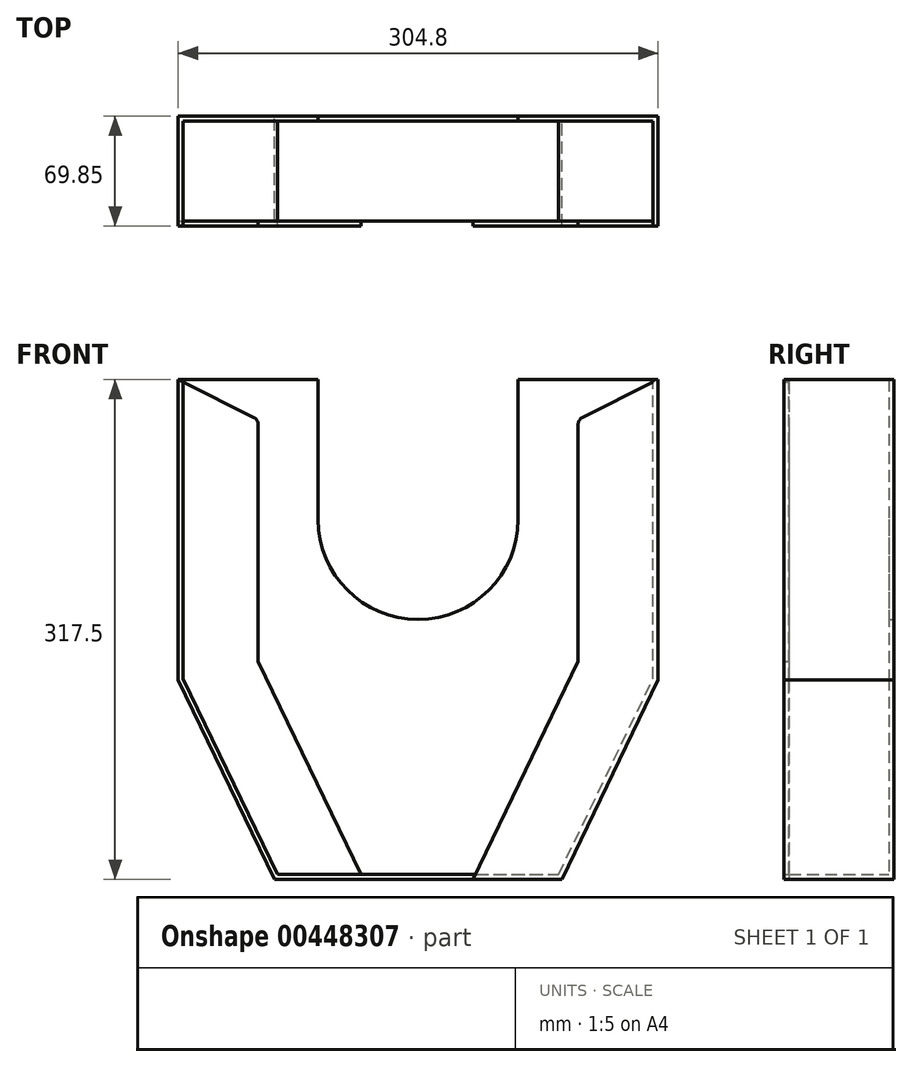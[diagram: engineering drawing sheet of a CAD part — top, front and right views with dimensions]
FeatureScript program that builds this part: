
annotation { "Feature Type Name" : "Feature", "Feature Type Description" : "" }
export const myFeature = defineFeature(function(context is Context, id is Id, definition is map)
    precondition{}
    {
        {
            var Q0;
            Q0=qCreatedBy(makeId("Front.planeOp"),FACE);
            var sketch = newSketch(context, id + "F0", { "sketchPlane" : qUnion([Q0])});
            skLineSegment(sketch, "E0", {"start": v(-244.47, 127.9) * mm, "end": v(-91.22, -189.6) * mm});
            skLineSegment(sketch, "E1", {"start": v(-91.22, -189.6) * mm, "end": v(91.22, -189.6) * mm});
            skLineSegment(sketch, "E2", {"start": v(91.22, -189.6) * mm, "end": v(244.47, 127.9) * mm});
            skLineSegment(sketch, "E3", {"start": v(244.48, 127.9) * mm, "end": v(-244.48, 127.9) * mm});
            skLineSegment(sketch, "E4.bottom", {"start": v(-63.5, 127.9) * mm, "end": v(63.5, 127.9) * mm});
            skLineSegment(sketch, "E4.top", {"start": v(-63.5, 39) * mm, "end": v(63.5, 39) * mm});
            skLineSegment(sketch, "E4.left", {"start": v(-63.5, 127.9) * mm, "end": v(-63.5, 39) * mm});
            skLineSegment(sketch, "E4.right", {"start": v(63.5, 127.9) * mm, "end": v(63.5, 39) * mm});
            skArc(sketch, "E5", {"start": v(-63.5, 39) * mm, "mid": v(0, -24.5) * mm, "end": v(63.5, 39) * mm});
            skCircle(sketch, "E6", {"center": v(0, -49.9) * mm, "radius": 139.7 * mm});
            skLineSegment(sketch, "E7", {"start": v(-152.4, -62.86) * mm, "end": v(-152.4, 127.9) * mm});
            skLineSegment(sketch, "E8", {"start": v(0, 127.9) * mm, "end": v(0, -189.6) * mm});
            skLineSegment(sketch, "E9.MirrorCS", {"start": v(152.4, -62.86) * mm, "end": v(152.4, 127.9) * mm});
            skSolve(sketch);
        }
        {
            var Q0;
            {var subQ1=sQuery(id+"F0.wireOp",EDGE,"E4.right");var subQ3=sQuery(id+"F0.wireOp",EDGE,"E6");var subQ4=makeQuery(id+"F0.imprint","INTERSECT",VERTEX,{"derivedFrom":[subQ1,subQ3]});Q0=makeQuery(id+"F0.imprint","IMPRINT",FACE,{"disambiguationData":[TD([[makeQuery(id+"F0.imprint","IMPRINT",EDGE,{"disambiguationData":[TD([[subQ4,-1.0]])],"derivedFrom":subQ1}),1.0]])]});}
            var Q1;
            {var subQ1=sQuery(id+"F0.wireOp",EDGE,"E4.left");var subQ3=sQuery(id+"F0.wireOp",EDGE,"E6");var subQ4=makeQuery(id+"F0.imprint","INTERSECT",VERTEX,{"derivedFrom":[subQ1,subQ3]});Q1=makeQuery(id+"F0.imprint","IMPRINT",FACE,{"disambiguationData":[TD([[makeQuery(id+"F0.imprint","IMPRINT",EDGE,{"disambiguationData":[TD([[subQ4,-1.0]])],"derivedFrom":subQ1}),-1.0]])]});}
            var Q2;
            {var subQ5=sQuery(id+"F0.wireOp",EDGE,"E7");Q2=makeQuery(id+"F0.imprint","IMPRINT",FACE,{"disambiguationData":[TD([[makeQuery(id+"F0.imprint","IMPRINT",EDGE,{"derivedFrom":subQ5}),-1.0]])]});}
            var Q3;
            {var subQ5=sQuery(id+"F0.wireOp",EDGE,"E9.MirrorCS");Q3=makeQuery(id+"F0.imprint","IMPRINT",FACE,{"disambiguationData":[TD([[makeQuery(id+"F0.imprint","IMPRINT",EDGE,{"derivedFrom":subQ5}),1.0]])]});}
            var Q4;
            {var subQ5=sQuery(id+"F0.wireOp",EDGE,"E7");Q4=makeQuery(id+"F0.imprint","IMPRINT",FACE,{"disambiguationData":[TD([[makeQuery(id+"F0.imprint","IMPRINT",EDGE,{"derivedFrom":subQ5}),-1.0]])]});}
            var Q5;
            {var subQ5=sQuery(id+"F0.wireOp",EDGE,"E9.MirrorCS");Q5=makeQuery(id+"F0.imprint","IMPRINT",FACE,{"disambiguationData":[TD([[makeQuery(id+"F0.imprint","IMPRINT",EDGE,{"derivedFrom":subQ5}),1.0]])]});}
            var Q6;
            {var subQ1=sQuery(id+"F0.wireOp",EDGE,"E4.right");var subQ3=sQuery(id+"F0.wireOp",EDGE,"E6");var subQ4=makeQuery(id+"F0.imprint","INTERSECT",VERTEX,{"derivedFrom":[subQ1,subQ3]});Q6=makeQuery(id+"F0.imprint","IMPRINT",FACE,{"disambiguationData":[TD([[makeQuery(id+"F0.imprint","IMPRINT",EDGE,{"disambiguationData":[TD([[subQ4,-1.0]])],"derivedFrom":subQ1}),1.0]])]});}
            extrude(context, id + "F1", {"entities" : qUnion([Q0, Q1, Q2, Q3, Q4, Q5, Q6]), "depth" : 3.17 * mm});
        }
        {
            var Q0;
            Q0=makeQuery(id+"F1.opExtrude","CAP_FACE",FACE,{"disambiguationData":[OSD([sQuery(id+"F0.wireOp",EDGE,"E0"),sQuery(id+"F0.wireOp",EDGE,"E1"),sQuery(id+"F0.wireOp",EDGE,"E2"),sQuery(id+"F0.wireOp",EDGE,"E3"),sQuery(id+"F0.wireOp",EDGE,"E4.left"),sQuery(id+"F0.wireOp",EDGE,"E4.right"),sQuery(id+"F0.wireOp",EDGE,"E5"),sQuery(id+"F0.wireOp",EDGE,"E7"),sQuery(id+"F0.wireOp",EDGE,"E9.MirrorCS")])],"isStart":false});
            var sketch = newSketch(context, id + "F2", { "sketchPlane" : qUnion([Q0])});
            skLineSegment(sketch, "E10", {"start": v(-149.23, 127.9) * mm, "end": v(-149.23, -62.13) * mm});
            skLineSegment(sketch, "E11", {"start": v(-149.23, -62.13) * mm, "end": v(-89.22, -186.43) * mm});
            skLineSegment(sketch, "E12", {"start": v(-89.22, -186.43) * mm, "end": v(89.22, -186.43) * mm});
            skLineSegment(sketch, "E13", {"start": v(89.22, -186.43) * mm, "end": v(149.22, -62.13) * mm});
            skLineSegment(sketch, "E14", {"start": v(149.22, -62.13) * mm, "end": v(149.22, 127.9) * mm});
            skLineSegment(sketch, "E15", {"start": v(149.22, 127.9) * mm, "end": v(152.4, 127.9) * mm});
            skLineSegment(sketch, "E16", {"start": v(152.4, 127.9) * mm, "end": v(152.4, -62.86) * mm});
            skLineSegment(sketch, "E17", {"start": v(152.4, -62.86) * mm, "end": v(91.22, -189.6) * mm});
            skLineSegment(sketch, "E18", {"start": v(91.22, -189.6) * mm, "end": v(-91.22, -189.6) * mm});
            skLineSegment(sketch, "E19", {"start": v(-91.22, -189.6) * mm, "end": v(-152.4, -62.86) * mm});
            skLineSegment(sketch, "E20", {"start": v(-152.4, -62.86) * mm, "end": v(-152.4, 127.9) * mm});
            skLineSegment(sketch, "E21", {"start": v(-152.4, 127.9) * mm, "end": v(-149.23, 127.9) * mm});
            skSolve(sketch);
        }
        {
            var Q0;
            Q0 = qSketchRegion(id + "F2", true);
            extrude(context, id + "F3", {"entities" : qUnion([Q0]), "operationType" : NewBodyOperationType.ADD, "depth" : 63.5 * mm});
        }
        {
            var Q0;
            Q0=makeQuery(id+"F3.opExtrude","CAP_FACE",FACE,{"disambiguationData":[OSD([sQuery(id+"F2.wireOp",EDGE,"E10"),sQuery(id+"F2.wireOp",EDGE,"E11"),sQuery(id+"F2.wireOp",EDGE,"E12"),sQuery(id+"F2.wireOp",EDGE,"E13"),sQuery(id+"F2.wireOp",EDGE,"E14"),sQuery(id+"F2.wireOp",EDGE,"E15"),sQuery(id+"F2.wireOp",EDGE,"E16"),sQuery(id+"F2.wireOp",EDGE,"E17"),sQuery(id+"F2.wireOp",EDGE,"E18"),sQuery(id+"F2.wireOp",EDGE,"E19"),sQuery(id+"F2.wireOp",EDGE,"E20"),sQuery(id+"F2.wireOp",EDGE,"E21")])],"isStart":false});
            var sketch = newSketch(context, id + "F4", { "sketchPlane" : qUnion([Q0])});
            skLineSegment(sketch, "E22", {"start": v(-152.4, 127.9) * mm, "end": v(-152.4, -62.86) * mm});
            skLineSegment(sketch, "E23", {"start": v(-152.4, -62.86) * mm, "end": v(-91.22, -189.6) * mm});
            skLineSegment(sketch, "E24", {"start": v(-91.22, -189.6) * mm, "end": v(91.22, -189.6) * mm});
            skLineSegment(sketch, "E25", {"start": v(91.22, -189.6) * mm, "end": v(152.4, -62.86) * mm});
            skLineSegment(sketch, "E26", {"start": v(152.4, -62.86) * mm, "end": v(152.4, 127.9) * mm});
            skLineSegment(sketch, "E27", {"start": v(152.4, 127.9) * mm, "end": v(101.6, 127.9) * mm});
            skLineSegment(sketch, "E28", {"start": v(101.6, 127.9) * mm, "end": v(101.6, -51.24) * mm});
            skLineSegment(sketch, "E29", {"start": v(101.6, -51.24) * mm, "end": v(59.33, -138.8) * mm});
            skLineSegment(sketch, "E30.MirrorCS", {"start": v(-101.6, -51.24) * mm, "end": v(-59.33, -138.8) * mm});
            skLineSegment(sketch, "E31.MirrorCS", {"start": v(-101.6, 127.9) * mm, "end": v(-101.6, -51.24) * mm});
            skLineSegment(sketch, "E32.MirrorCS", {"start": v(-152.4, 127.9) * mm, "end": v(-101.6, 127.9) * mm});
            skLineSegment(sketch, "E33.MirrorCS", {"start": v(-152.4, -62.86) * mm, "end": v(-152.4, 127.9) * mm});
            skLineSegment(sketch, "E34.MirrorCS", {"start": v(-91.22, -189.6) * mm, "end": v(-152.4, -62.86) * mm});
            skLineSegment(sketch, "E35.MirrorCS", {"start": v(91.22, -189.6) * mm, "end": v(-91.22, -189.6) * mm});
            skLineSegment(sketch, "E36", {"start": v(-152.4, 127.9) * mm, "end": v(-101.6, 102.5) * mm});
            skLineSegment(sketch, "E37.MirrorCS", {"start": v(152.4, 127.9) * mm, "end": v(101.6, 102.5) * mm});
            skLineSegment(sketch, "E38", {"start": v(-59.33, -138.8) * mm, "end": v(-34.8, -189.6) * mm});
            skLineSegment(sketch, "E39", {"start": v(59.33, -138.8) * mm, "end": v(34.8, -189.6) * mm});
            skLineSegment(sketch, "E40", {"start": v(-91.22, -189.6) * mm, "end": v(-34.8, -189.6) * mm});
            skSolve(sketch);
        }
        {
            var Q0;
            {var subQ0=sQuery(id+"F4.wireOp",EDGE,"E29");Q0=makeQuery(id+"F4.imprint","IMPRINT",FACE,{"disambiguationData":[TD([[makeQuery(id+"F4.imprint","IMPRINT",EDGE,{"derivedFrom":subQ0}),1.0]])]});}
            var Q1;
            {var subQ5=sQuery(id+"F4.wireOp",EDGE,"E30.MirrorCS");Q1=makeQuery(id+"F4.imprint","IMPRINT",FACE,{"disambiguationData":[TD([[makeQuery(id+"F4.imprint","IMPRINT",EDGE,{"derivedFrom":subQ5}),-1.0]])]});}
            var Q2;
            Q2=makeQuery(id+"F4.imprint","IMPRINT",FACE,{"disambiguationData":[TD([[makeQuery(id+"F4.imprint","IMPRINT",EDGE,{"derivedFrom":sQuery(id+"F4.wireOp",EDGE,"E25")}),1.0]])]});
            var Q3;
            {var subQ5=sQuery(id+"F4.wireOp",EDGE,"E33.MirrorCS");Q3=makeQuery(id+"F4.imprint","IMPRINT",FACE,{"disambiguationData":[TD([[makeQuery(id+"F4.imprint","IMPRINT",EDGE,{"derivedFrom":subQ5}),-1.0]])]});}
            var Q4;
            {var subQ1=sQuery(id+"F4.wireOp",EDGE,"E27");var subQ3=makeQuery(id+"F3.opExtrude","CAP_EDGE",EDGE,{"disambiguationData":[OSD([sQuery(id+"F2.wireOp",EDGE,"E14")])],"isStart":false});var subQ4=makeQuery(id+"F4.imprint","INTERSECT",VERTEX,{"derivedFrom":[subQ3,subQ1]});Q4=makeQuery(id+"F4.imprint","IMPRINT",FACE,{"disambiguationData":[TD([[makeQuery(id+"F4.imprint","IMPRINT",EDGE,{"disambiguationData":[TD([[subQ4,1.0]])],"derivedFrom":subQ3}),-1.0]])]});}
            var Q5;
            {var subQ1=sQuery(id+"F4.wireOp",EDGE,"E32.MirrorCS");var subQ3=makeQuery(id+"F3.opExtrude","CAP_EDGE",EDGE,{"disambiguationData":[OSD([sQuery(id+"F2.wireOp",EDGE,"E10")])],"isStart":false});var subQ4=makeQuery(id+"F4.imprint","INTERSECT",VERTEX,{"derivedFrom":[subQ3,subQ1]});Q5=makeQuery(id+"F4.imprint","IMPRINT",FACE,{"disambiguationData":[TD([[makeQuery(id+"F4.imprint","IMPRINT",EDGE,{"disambiguationData":[TD([[subQ4,-1.0]])],"derivedFrom":subQ3}),-1.0]])]});}
            extrude(context, id + "F5", {"entities" : qUnion([Q0, Q1, Q2, Q3, Q4, Q5]), "operationType" : NewBodyOperationType.ADD, "depth" : 3.17 * mm});
        }
        {
            var Q0;
            Q0=makeQuery(id+"F5.opExtrude","SWEPT_EDGE",EDGE,{"disambiguationData":[OSD([sQuery(id+"F4.wireOp",EDGE,"E28"),sQuery(id+"F4.wireOp",EDGE,"E37.MirrorCS")])]});
            var Q1;
            Q1=makeQuery(id+"F5.opExtrude","SWEPT_EDGE",EDGE,{"disambiguationData":[OSD([sQuery(id+"F4.wireOp",EDGE,"E31.MirrorCS"),sQuery(id+"F4.wireOp",EDGE,"E36")])]});
            fillet(context, id + "F6", {"entities" : qUnion([Q0, Q1]), "radius" : 5.08 * mm, "tangentPropagation" : true, "allowEdgeOverflow" : false});
        }
    });
